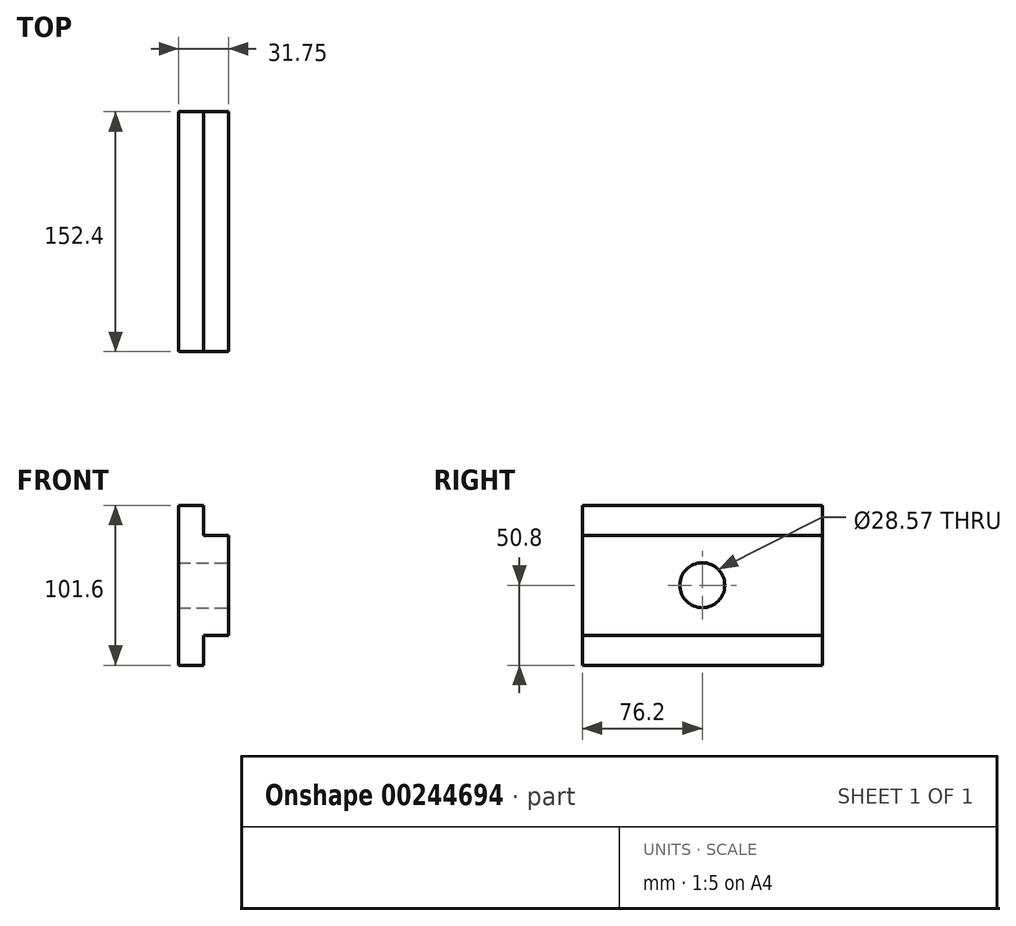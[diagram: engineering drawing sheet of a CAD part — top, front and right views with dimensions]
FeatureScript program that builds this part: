
annotation { "Feature Type Name" : "Feature", "Feature Type Description" : "" }
export const myFeature = defineFeature(function(context is Context, id is Id, definition is map)
    precondition{}
    {
        {
            var Q0;
            Q0=qCreatedBy(makeId("Front.planeOp"),FACE);
            var sketch = newSketch(context, id + "F0", { "sketchPlane" : qUnion([Q0])});
            skLineSegment(sketch, "E0", {"start": v(0, 0) * mm, "end": v(0, 101.6) * mm});
            skLineSegment(sketch, "E1", {"start": v(0, 0) * mm, "end": v(15.88, 0) * mm});
            skLineSegment(sketch, "E2", {"start": v(15.88, 0) * mm, "end": v(15.88, 19.05) * mm});
            skLineSegment(sketch, "E3", {"start": v(15.88, 19.05) * mm, "end": v(31.75, 19.05) * mm});
            skLineSegment(sketch, "E4", {"start": v(31.75, 19.05) * mm, "end": v(31.75, 82.55) * mm});
            skLineSegment(sketch, "E5", {"start": v(31.75, 82.55) * mm, "end": v(15.88, 82.55) * mm});
            skLineSegment(sketch, "E6", {"start": v(15.88, 82.55) * mm, "end": v(15.88, 101.6) * mm});
            skLineSegment(sketch, "E7", {"start": v(15.88, 101.6) * mm, "end": v(0, 101.6) * mm});
            skSolve(sketch);
        }
        {
            var Q0;
            Q0=makeQuery(id+"F0.imprint","IMPRINT",FACE,{"disambiguationData":[TD([[makeQuery(id+"F0.imprint","IMPRINT",EDGE,{"derivedFrom":sQuery(id+"F0.wireOp",EDGE,"E0")}),-1.0]])]});
            extrude(context, id + "F1", {"entities" : qUnion([Q0]), "oppositeDirection" : true, "depth" : 152.4 * mm});
        }
        {
            var Q0;
            Q0=makeQuery(id+"F1.opExtrude","SWEPT_FACE",FACE,{"disambiguationData":[OSD([sQuery(id+"F0.wireOp",EDGE,"E4")])]});
            var sketch = newSketch(context, id + "F2", { "sketchPlane" : qUnion([Q0])});
            skCircle(sketch, "E8", {"center": v(76.2, 50.8) * mm, "radius": 14.29 * mm});
            skPoint(sketch, "E9.orphan", {"position": v(76.2, 82.55) * mm});
            skPoint(sketch, "E10.orphan", {"position": v(76.2, 19.05) * mm});
            skSolve(sketch);
        }
        {
            var Q0;
            Q0=makeQuery(id+"F2.imprint","IMPRINT",FACE,{"disambiguationData":[TD([[makeQuery(id+"F2.imprint","IMPRINT",EDGE,{"derivedFrom":sQuery(id+"F2.wireOp",EDGE,"E8")}),1.0]])]});
            extrude(context, id + "F3", {"entities" : qUnion([Q0]), "operationType" : NewBodyOperationType.REMOVE, "oppositeDirection" : true, "depth" : 31.75 * mm});
        }
    });
